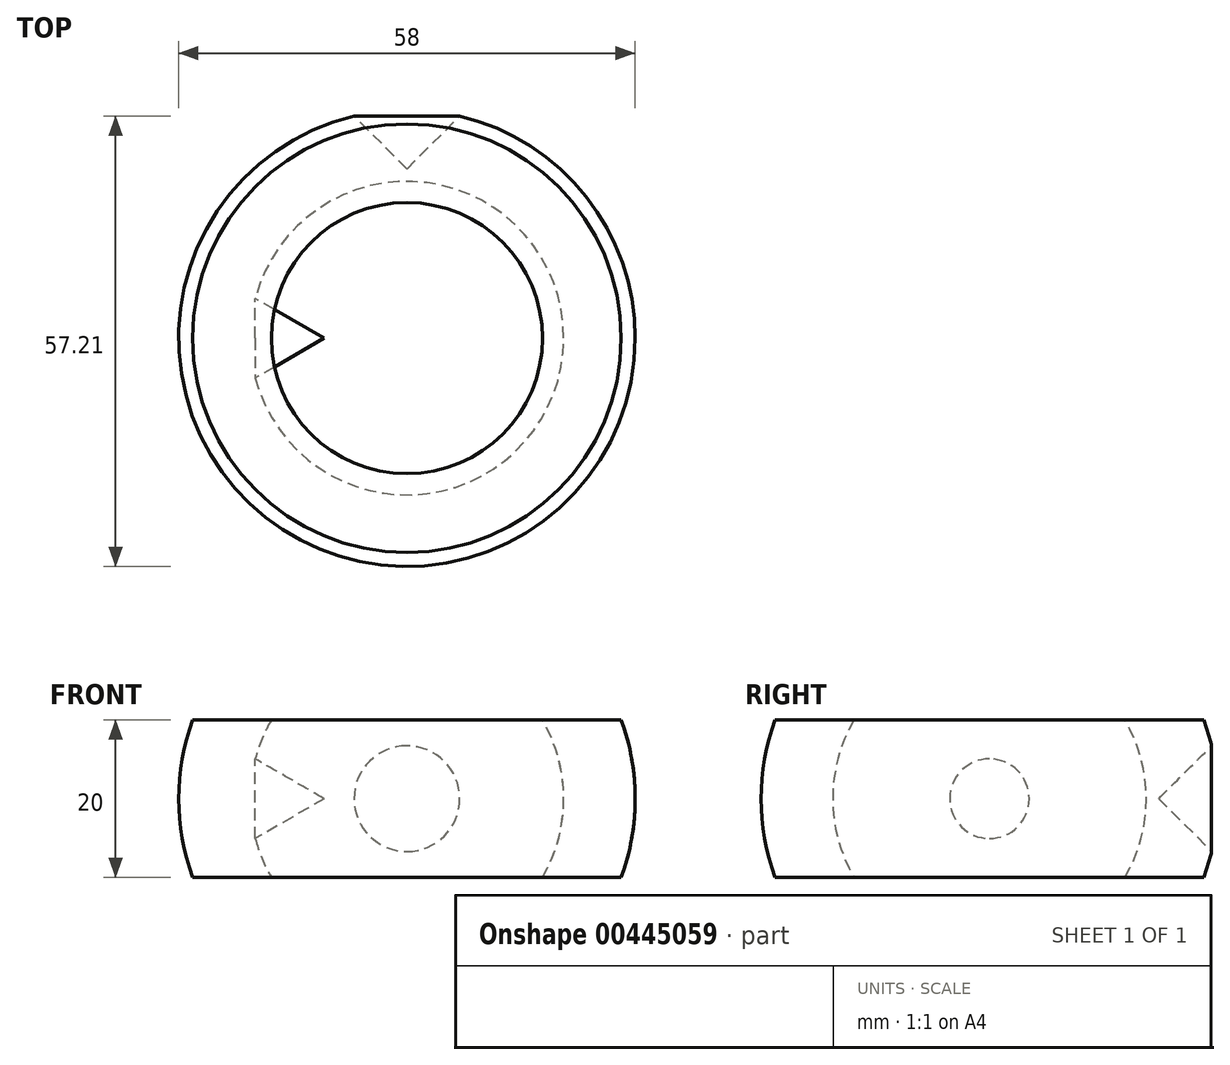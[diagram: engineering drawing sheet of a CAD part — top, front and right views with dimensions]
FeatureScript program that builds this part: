
annotation { "Feature Type Name" : "Feature", "Feature Type Description" : "" }
export const myFeature = defineFeature(function(context is Context, id is Id, definition is map)
    precondition{}
    {
        {
            var Q0;
            Q0=qCreatedBy(makeId("Front.planeOp"),FACE);
            var sketch = newSketch(context, id + "F0", { "sketchPlane" : qUnion([Q0])});
            skArc(sketch, "E0", {"start": v(17.22, 10) * mm, "mid": v(19.91, 0) * mm, "end": v(17.22, -10) * mm});
            skArc(sketch, "E1", {"start": v(27.22, 10) * mm, "mid": v(29, 0) * mm, "end": v(27.22, -10) * mm});
            skLineSegment(sketch, "E2", {"start": v(17.22, 10) * mm, "end": v(27.22, 10) * mm});
            skLineSegment(sketch, "E3", {"start": v(17.22, -10) * mm, "end": v(27.22, -10) * mm});
            skLineSegment(sketch, "E4", {"start": v(27.22, 10) * mm, "end": v(27.22, -10) * mm});
            skPoint(sketch, "E5", {"position": v(27.22, 0) * mm});
            skLineSegment(sketch, "E6", {"start": v(0, 5.08) * mm, "end": v(0, -5.1) * mm});
            skSolve(sketch);
        }
        {
            var Q0;
            Q0=qSketchRegion(id+"F0",true);
            var Q1;
            Q1=sQuery(id+"F0.wireOp",EDGE,"E6");
            revolve(context, id + "F1", {"entities" : qUnion([Q0]), "axis" : qUnion([Q1]), "revolveType" : RevolveType.FULL});
        }
        {
            var Q0;
            Q0=qCreatedBy(makeId("Top.planeOp"),FACE);
            var sketch = newSketch(context, id + "F2", { "sketchPlane" : qUnion([Q0])});
            skLineSegment(sketch, "E7", {"start": v(0, 21.5) * mm, "end": v(9, 30.5) * mm});
            skLineSegment(sketch, "E8", {"start": v(9, 30.5) * mm, "end": v(-9, 30.5) * mm});
            skLineSegment(sketch, "E9", {"start": v(-9, 30.5) * mm, "end": v(0, 21.5) * mm});
            skLineSegment(sketch, "E10", {"start": v(0, 30.5) * mm, "end": v(0, 21.5) * mm});
            skSolve(sketch);
        }
        {
            var Q0;
            {var subQ0=sQuery(id+"F2.wireOp",EDGE,"E7");Q0=makeQuery(id+"F2.imprint","IMPRINT",FACE,{"disambiguationData":[TD([[makeQuery(id+"F2.imprint","IMPRINT",EDGE,{"derivedFrom":subQ0}),1.0]])]});}
            var Q1;
            Q1=sQuery(id+"F2.wireOp",EDGE,"E10");
            revolve(context, id + "F3", {"operationType" : NewBodyOperationType.REMOVE, "entities" : qUnion([Q0]), "axis" : qUnion([Q1]), "revolveType" : RevolveType.FULL, "oppositeDirection" : true});
        }
        {
            var Q0;
            Q0=qCreatedBy(makeId("Top.planeOp"),FACE);
            var sketch = newSketch(context, id + "F4", { "sketchPlane" : qUnion([Q0])});
            skLineSegment(sketch, "E11", {"start": v(-23.5, 7.5) * mm, "end": v(-23.5, -7.5) * mm});
            skLineSegment(sketch, "E12", {"start": v(-23.5, -7.5) * mm, "end": v(-10.5, 0) * mm});
            skLineSegment(sketch, "E13", {"start": v(-10.5, 0) * mm, "end": v(-23.5, 7.5) * mm});
            skLineSegment(sketch, "E14", {"start": v(-10.5, 0) * mm, "end": v(-23.5, 0) * mm});
            skSolve(sketch);
        }
        {
            var Q0;
            {var subQ0=sQuery(id+"F4.wireOp",EDGE,"E13");Q0=makeQuery(id+"F4.imprint","IMPRINT",FACE,{"disambiguationData":[TD([[makeQuery(id+"F4.imprint","IMPRINT",EDGE,{"derivedFrom":subQ0}),1.0]])]});}
            var Q1;
            Q1=sQuery(id+"F4.wireOp",EDGE,"E14");
            revolve(context, id + "F5", {"operationType" : NewBodyOperationType.ADD, "entities" : qUnion([Q0]), "axis" : qUnion([Q1]), "revolveType" : RevolveType.FULL});
        }
    });
